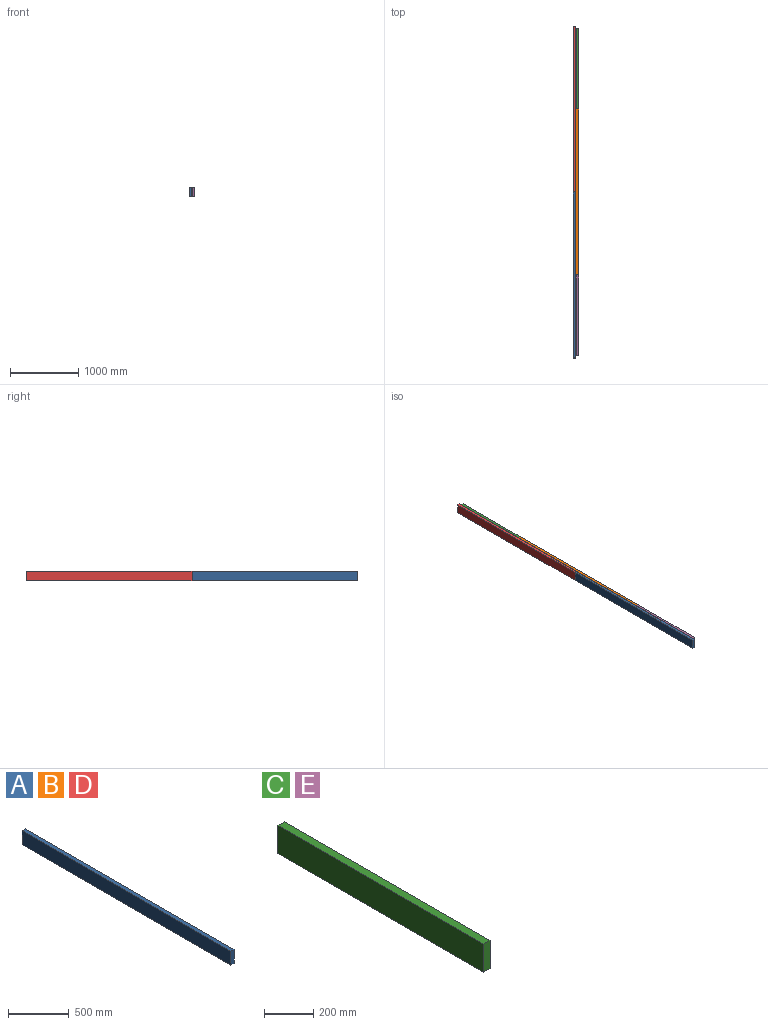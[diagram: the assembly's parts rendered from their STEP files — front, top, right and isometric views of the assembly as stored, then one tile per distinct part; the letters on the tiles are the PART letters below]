
ASSEMBLY  parts=5 mates=4
PART A: 6 faces, bbox 38.1x2438.4x139.7 mm
  f0: plane 2438.4x139.7mm, normal (-1,0,0), area 340644.5mm2, adj f1,f3,f4,f5
  f1: plane 2438.4x38.1mm, normal (0,0,-1), area 92903mm2, adj f0,f2,f4,f5
  f2: plane 2438.4x139.7mm, normal (1,0,0), area 340644.5mm2, adj f1,f3,f4,f5
  f3: plane 2438.4x38.1mm, normal (0,0,1), area 92903mm2, adj f0,f2,f4,f5
  f4: plane 139.7x38.1mm, normal (0,1,0), area 5322.6mm2, adj f0,f1,f2,f3
  f5: plane 139.7x38.1mm, normal (0,-1,0), area 5322.6mm2, adj f0,f1,f2,f3
PART B: same geometry as A
PART C: 6 faces, bbox 38.1x1181.1x139.7 mm
  f0: plane 1181.1x38.1mm, normal (0,0,-1), area 44999.9mm2, adj f1,f3,f4,f5
  f1: plane 1181.1x139.7mm, normal (1,0,0), area 164999.7mm2, adj f0,f2,f4,f5
  f2: plane 1181.1x38.1mm, normal (0,0,1), area 44999.9mm2, adj f1,f3,f4,f5
  f3: plane 1181.1x139.7mm, normal (-1,0,0), area 164999.7mm2, adj f0,f2,f4,f5
  f4: plane 139.7x38.1mm, normal (0,1,0), area 5322.6mm2, adj f0,f1,f2,f3
  f5: plane 139.7x38.1mm, normal (0,-1,0), area 5322.6mm2, adj f0,f1,f2,f3
PART D: same geometry as A
PART E: same geometry as C
PLACE A t=(-2232.32,-1074.79,-344.73)mm
PLACE B t=(-2194.22,144.41,-344.73)mm
PLACE C t=(-2028.76,2582.81,-344.73)mm
PLACE D t=(-2232.32,1363.61,-344.73)mm
PLACE E t=(-2028.76,-1036.69,-344.73)mm
MATE fastened B.f3 <-> D.f3  axis (0,0,1) through (-2194.22,1363.61,-205.03)mm
MATE fastened C.f2 <-> B.f3  axis (0,0,1) through (-2194.22,2582.81,-205.03)mm
MATE fastened E.f2 <-> B.f3  axis (0,0,1) through (-2156.12,144.41,-205.03)mm
MATE fastened A.f1 <-> D.f1  axis (0,0,1) through (-2194.22,1363.61,-344.73)mm
